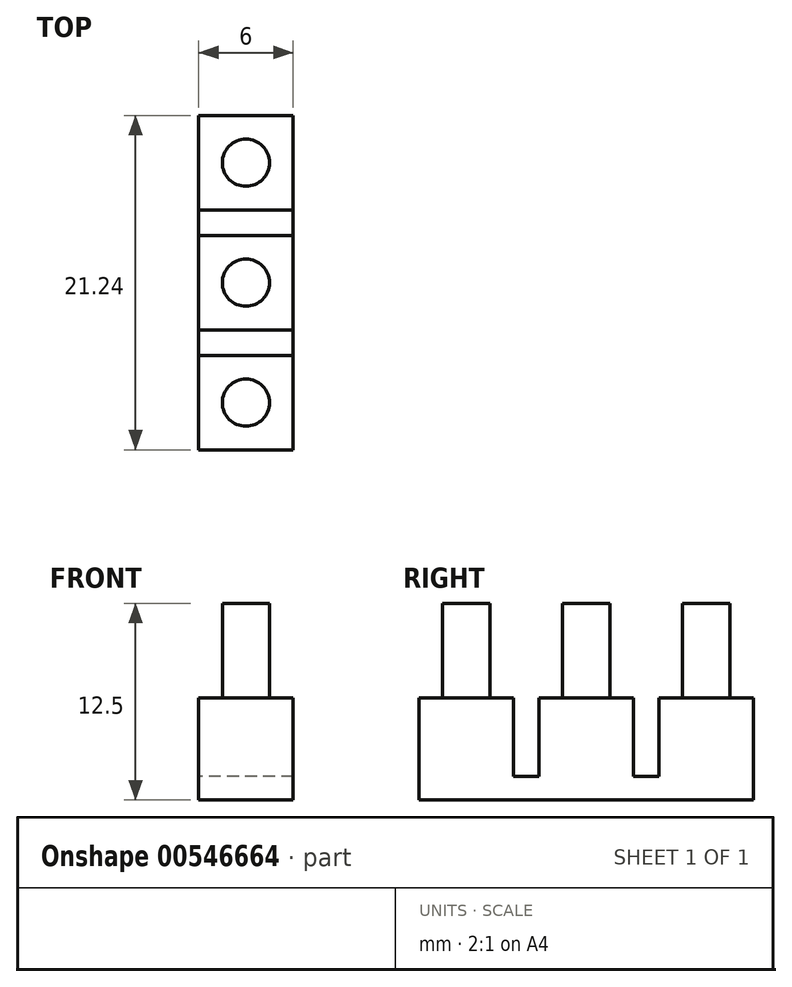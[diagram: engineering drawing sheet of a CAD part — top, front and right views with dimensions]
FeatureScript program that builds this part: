
annotation { "Feature Type Name" : "Feature", "Feature Type Description" : "" }
export const myFeature = defineFeature(function(context is Context, id is Id, definition is map)
    precondition{}
    {
        {
            var Q0;
            Q0=qCreatedBy(makeId("Top.planeOp"),FACE);
            var sketch = newSketch(context, id + "F0", { "sketchPlane" : qUnion([Q0])});
            skLineSegment(sketch, "E0.bottom", {"start": v(3, -10.62) * mm, "end": v(-3, -10.62) * mm});
            skLineSegment(sketch, "E0.top", {"start": v(3, 10.62) * mm, "end": v(-3, 10.62) * mm});
            skLineSegment(sketch, "E0.left", {"start": v(3, -10.62) * mm, "end": v(3, 10.62) * mm});
            skLineSegment(sketch, "E0.right", {"start": v(-3, -10.62) * mm, "end": v(-3, 10.62) * mm});
            skPoint(sketch, "E0.middle", {"position": v(0, 0) * mm});
            skSolve(sketch);
        }
        {
            var Q0;
            Q0 = qSketchRegion(id + "F0", true);
            extrude(context, id + "F1", {"entities" : qUnion([Q0]), "depth" : 1.5 * mm, "offsetDistance" : 25 * mm});
        }
        {
            var Q0;
            Q0=makeQuery(id+"F1.opExtrude","CAP_FACE",FACE,{"disambiguationData":[OSD([sQuery(id+"F0.wireOp",EDGE,"E0.bottom"),sQuery(id+"F0.wireOp",EDGE,"E0.top"),sQuery(id+"F0.wireOp",EDGE,"E0.left"),sQuery(id+"F0.wireOp",EDGE,"E0.right")])],"isStart":false});
            var sketch = newSketch(context, id + "F2", { "sketchPlane" : qUnion([Q0])});
            skLineSegment(sketch, "E1.bottom", {"start": v(3, 4.62) * mm, "end": v(-3, 4.62) * mm});
            skLineSegment(sketch, "E1.top", {"start": v(3, 10.62) * mm, "end": v(-3, 10.62) * mm});
            skLineSegment(sketch, "E1.left", {"start": v(3, 4.62) * mm, "end": v(3, 10.62) * mm});
            skLineSegment(sketch, "E1.right", {"start": v(-3, 4.62) * mm, "end": v(-3, 10.62) * mm});
            skPoint(sketch, "E1.middle", {"position": v(0, 7.62) * mm});
            skPoint(sketch, "E1.middle.positionSnap0", {"position": v(0, -10.62) * mm});
            skPoint(sketch, "E1.centerSnap0", {"position": v(0, -10.62) * mm});
            skLineSegment(sketch, "E2.0.1.0", {"start": v(3, 3) * mm, "end": v(-3, 3) * mm});
            skLineSegment(sketch, "E2.0.1.1", {"start": v(3, -3) * mm, "end": v(3, 3) * mm});
            skLineSegment(sketch, "E2.0.1.2", {"start": v(3, -3) * mm, "end": v(-3, -3) * mm});
            skLineSegment(sketch, "E2.0.1.3", {"start": v(-3, -3) * mm, "end": v(-3, 3) * mm});
            skLineSegment(sketch, "E2.0.2.0", {"start": v(3, -4.62) * mm, "end": v(-3, -4.62) * mm});
            skLineSegment(sketch, "E2.0.2.1", {"start": v(3, -10.62) * mm, "end": v(3, -4.62) * mm});
            skLineSegment(sketch, "E2.0.2.2", {"start": v(3, -10.62) * mm, "end": v(-3, -10.62) * mm});
            skLineSegment(sketch, "E2.0.2.3", {"start": v(-3, -10.62) * mm, "end": v(-3, -4.62) * mm});
            skLineSegment(sketch, "E2.direction1", {"start": v(-3, 4.62) * mm, "end": v(22, 4.62) * mm, "construction": true});
            skLineSegment(sketch, "E2.direction2", {"start": v(-3, 4.62) * mm, "end": v(-3, -3) * mm, "construction": true});
            skSolve(sketch);
        }
        {
            var Q0;
            Q0 = qSketchRegion(id + "F2", true);
            extrude(context, id + "F3", {"entities" : qUnion([Q0]), "operationType" : NewBodyOperationType.ADD, "depth" : 5 * mm, "offsetDistance" : 25 * mm});
        }
        {
            var Q0;
            Q0=makeQuery(id+"F3.opExtrude","CAP_FACE",FACE,{"disambiguationData":[OSD([sQuery(id+"F2.wireOp",EDGE,"E2.0.1.0"),sQuery(id+"F2.wireOp",EDGE,"E2.0.1.1"),sQuery(id+"F2.wireOp",EDGE,"E2.0.1.2"),sQuery(id+"F2.wireOp",EDGE,"E2.0.1.3")])],"isStart":false});
            var sketch = newSketch(context, id + "F4", { "sketchPlane" : qUnion([Q0])});
            skCircle(sketch, "E3", {"center": v(0, 0) * mm, "radius": 1.5 * mm});
            skPoint(sketch, "E3.centerSnap0", {"position": v(0, -3) * mm});
            skPoint(sketch, "E3.centerSnap1", {"position": v(3, 0) * mm});
            skCircle(sketch, "E4.0.1.0", {"center": v(0, 7.62) * mm, "radius": 1.5 * mm});
            skLineSegment(sketch, "E4.direction2", {"start": v(0, 0) * mm, "end": v(0, 7.62) * mm, "construction": true});
            skCircle(sketch, "E5.0.1.0", {"center": v(0, -7.62) * mm, "radius": 1.5 * mm});
            skLineSegment(sketch, "E5.direction2", {"start": v(0, 0) * mm, "end": v(0, -7.62) * mm, "construction": true});
            skSolve(sketch);
        }
        {
            var Q0;
            Q0 = qSketchRegion(id + "F4", true);
            extrude(context, id + "F5", {"entities" : qUnion([Q0]), "operationType" : NewBodyOperationType.ADD, "depth" : 6 * mm, "offsetDistance" : 25 * mm});
        }
    });
